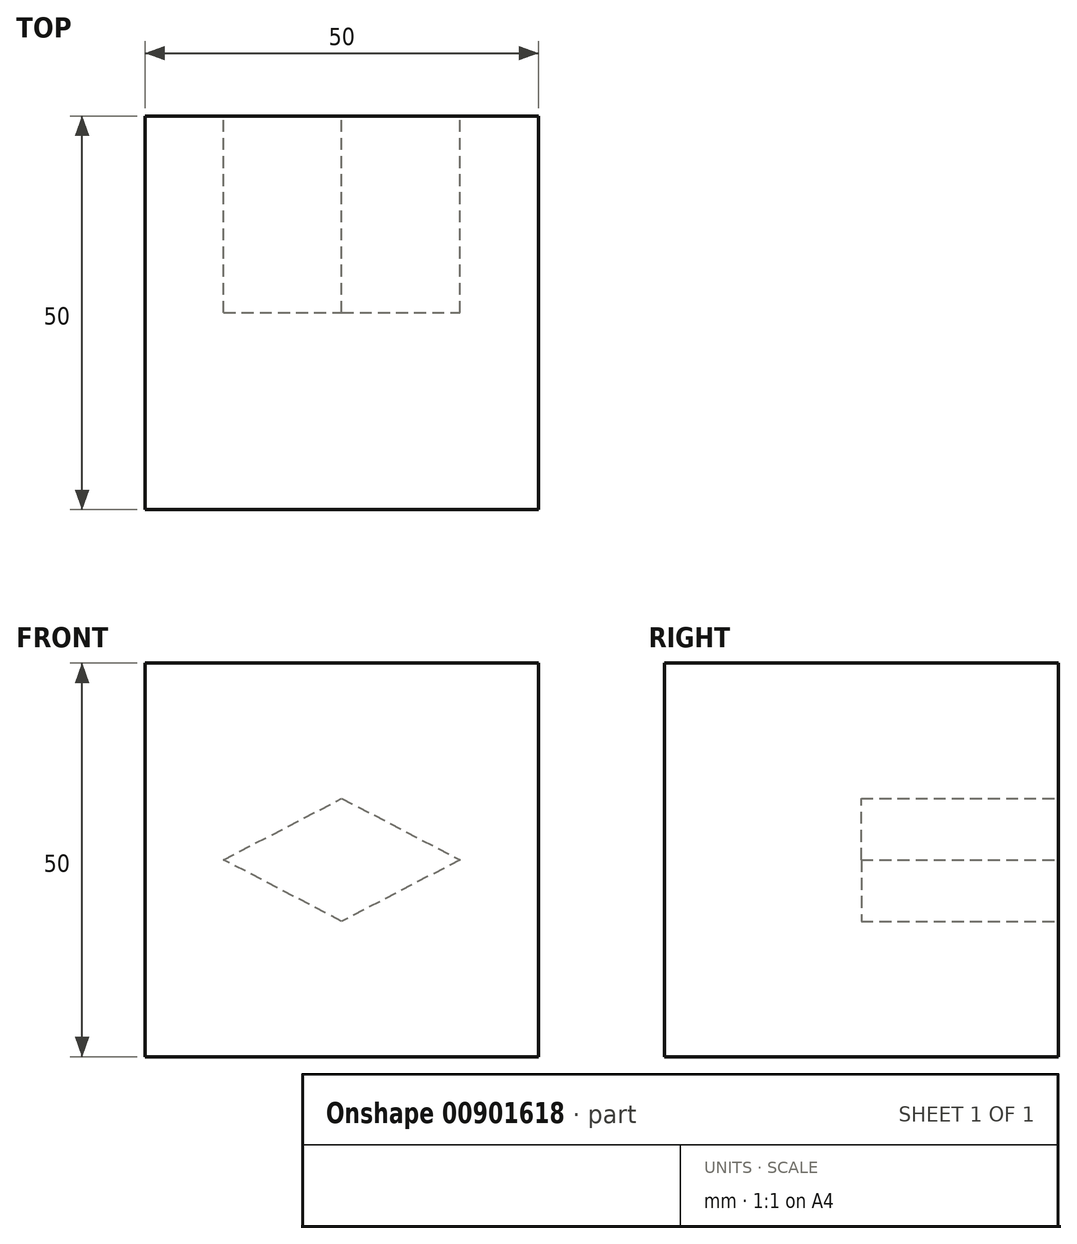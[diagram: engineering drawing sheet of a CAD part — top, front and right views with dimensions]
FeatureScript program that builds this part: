
annotation { "Feature Type Name" : "Feature", "Feature Type Description" : "" }
export const myFeature = defineFeature(function(context is Context, id is Id, definition is map)
    precondition{}
    {
        {
            var Q0;
            Q0=qCreatedBy(makeId("Front.planeOp"),FACE);
            var sketch = newSketch(context, id + "F0", { "sketchPlane" : qUnion([Q0])});
            skLineSegment(sketch, "E0.bottom", {"start": v(25, 25) * mm, "end": v(-25, 25) * mm});
            skLineSegment(sketch, "E0.top", {"start": v(25, -25) * mm, "end": v(-25, -25) * mm});
            skLineSegment(sketch, "E0.left", {"start": v(25, 25) * mm, "end": v(25, -25) * mm});
            skLineSegment(sketch, "E0.right", {"start": v(-25, 25) * mm, "end": v(-25, -25) * mm});
            skPoint(sketch, "E0.middle", {"position": v(0, 0) * mm});
            skSolve(sketch);
        }
        {
            var Q0;
            Q0 = qSketchRegion(id + "F0", true);
            extrude(context, id + "F1", {"entities" : qUnion([Q0]), "endBound" : BoundingType.SYMMETRIC, "depth" : 50 * mm, "offsetDistance" : 25 * mm});
        }
        {
            var Q0;
            Q0=makeQuery(id+"F1.opExtrude","CAP_FACE",FACE,{"disambiguationData":[OSD([sQuery(id+"F0.wireOp",EDGE,"E0.bottom"),sQuery(id+"F0.wireOp",EDGE,"E0.top"),sQuery(id+"F0.wireOp",EDGE,"E0.left"),sQuery(id+"F0.wireOp",EDGE,"E0.right")])],"isStart":true});
            var sketch = newSketch(context, id + "F2", { "sketchPlane" : qUnion([Q0])});
            skLineSegment(sketch, "E1", {"start": v(0, 7.8) * mm, "end": v(-15, 0) * mm});
            skLineSegment(sketch, "E2", {"start": v(-15, 0) * mm, "end": v(0, -7.8) * mm});
            skLineSegment(sketch, "E3", {"start": v(0, -7.8) * mm, "end": v(15, 0) * mm});
            skLineSegment(sketch, "E4", {"start": v(15, 0) * mm, "end": v(0, 7.8) * mm});
            skSolve(sketch);
        }
        {
            var Q0;
            Q0 = qSketchRegion(id + "F2", true);
            extrude(context, id + "F3", {"entities" : qUnion([Q0]), "operationType" : NewBodyOperationType.REMOVE, "oppositeDirection" : true, "depth" : 25 * mm, "offsetDistance" : 25 * mm});
        }
    });
